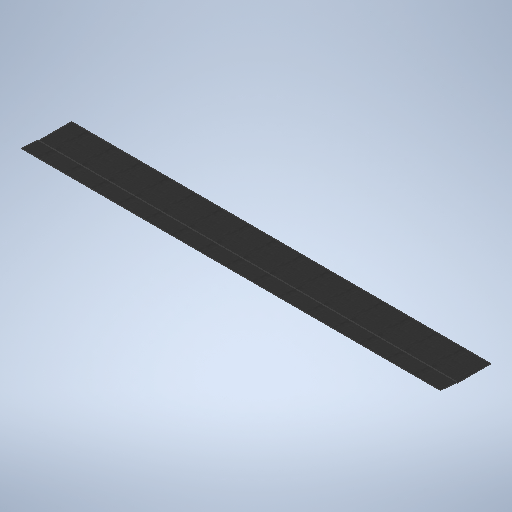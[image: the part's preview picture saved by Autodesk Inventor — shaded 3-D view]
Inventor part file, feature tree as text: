
AUTODESK INVENTOR PART (.ipt)
format: ipt  version: 2025.1 (Build 291241020, 241B)  size: 268,288 bytes
history: native  units: in
note: dims shown in document units (in); Inventor stores cm internally (conversion verified against a paired STEP export)
features: extrude x1, sketch x1
ambient origin geometry x8: Origin, YZ Plane, XZ Plane, XY Plane, X Axis, Y Axis, Z Axis, Center Point
bodies: Solid1 (feature_tree)
feature tree (2):
  extrude  "Extrusion1"  Depth=0.125in
  sketch  "Sketch1"  dims[d0=23.408in d1=0.125in d2=0.265in d7=0.125in d8=0.237in d9=1.1431in d10=0.125in d11=0.7449in d12=0.125in d13=12.09in d14=295.075in d15=0.0in]
